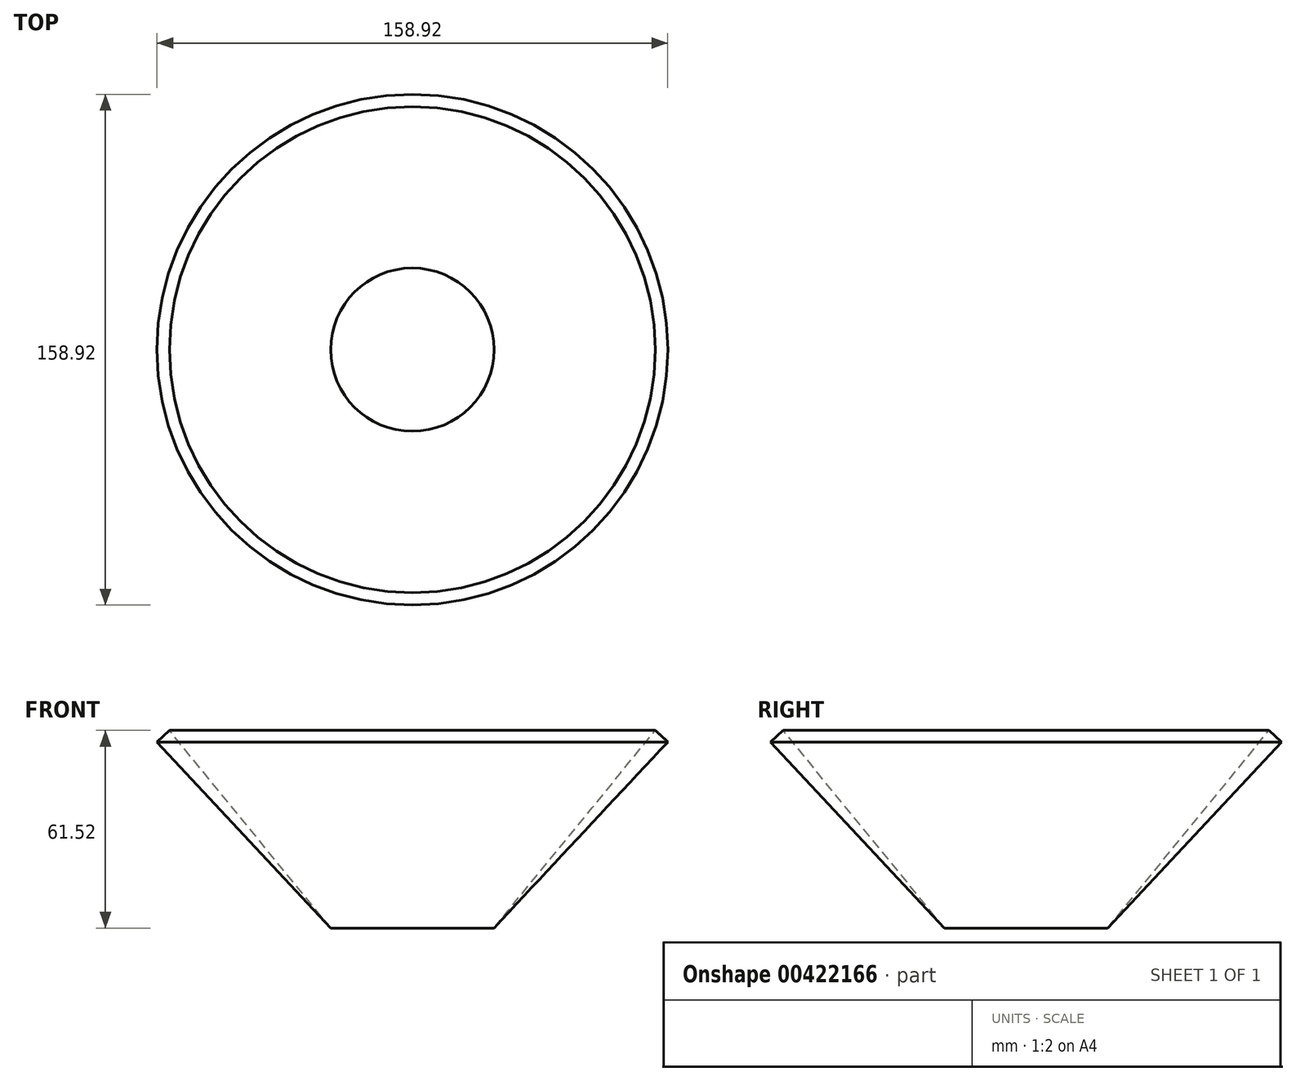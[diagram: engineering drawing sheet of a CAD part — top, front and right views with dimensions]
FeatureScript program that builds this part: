
annotation { "Feature Type Name" : "Feature", "Feature Type Description" : "" }
export const myFeature = defineFeature(function(context is Context, id is Id, definition is map)
    precondition{}
    {
        {
            var Q0;
            Q0=qCreatedBy(makeId("Front.planeOp"),FACE);
            var sketch = newSketch(context, id + "F0", { "sketchPlane" : qUnion([Q0])});
            skLineSegment(sketch, "E0", {"start": v(0, 0) * mm, "end": v(0, -25.4) * mm});
            skLineSegment(sketch, "E1", {"start": v(0, 0) * mm, "end": v(-25.4, 0) * mm});
            skLineSegment(sketch, "E2", {"start": v(-25.4, 0) * mm, "end": v(-25.4, -25.4) * mm});
            skLineSegment(sketch, "E3", {"start": v(-25.4, -25.4) * mm, "end": v(0, -25.4) * mm});
            skLineSegment(sketch, "E4", {"start": v(0, 0) * mm, "end": v(54.06, 57.91) * mm});
            skLineSegment(sketch, "E5", {"start": v(54.06, 57.91) * mm, "end": v(50.2, 61.52) * mm});
            skLineSegment(sketch, "E6", {"start": v(50.2, 61.52) * mm, "end": v(0, 0) * mm});
            skSolve(sketch);
        }
        {
            var Q0;
            Q0=makeQuery(id+"F0.imprint","IMPRINT",FACE,{"disambiguationData":[TD([[makeQuery(id+"F0.imprint","IMPRINT",EDGE,{"derivedFrom":sQuery(id+"F0.wireOp",EDGE,"E4")}),1.0]])]});
            var Q1;
            Q1=sQuery(id+"F0.wireOp",EDGE,"E2");
            revolve(context, id + "F1", {"entities" : qUnion([Q0]), "axis" : qUnion([Q1]), "revolveType" : RevolveType.FULL});
        }
    });
